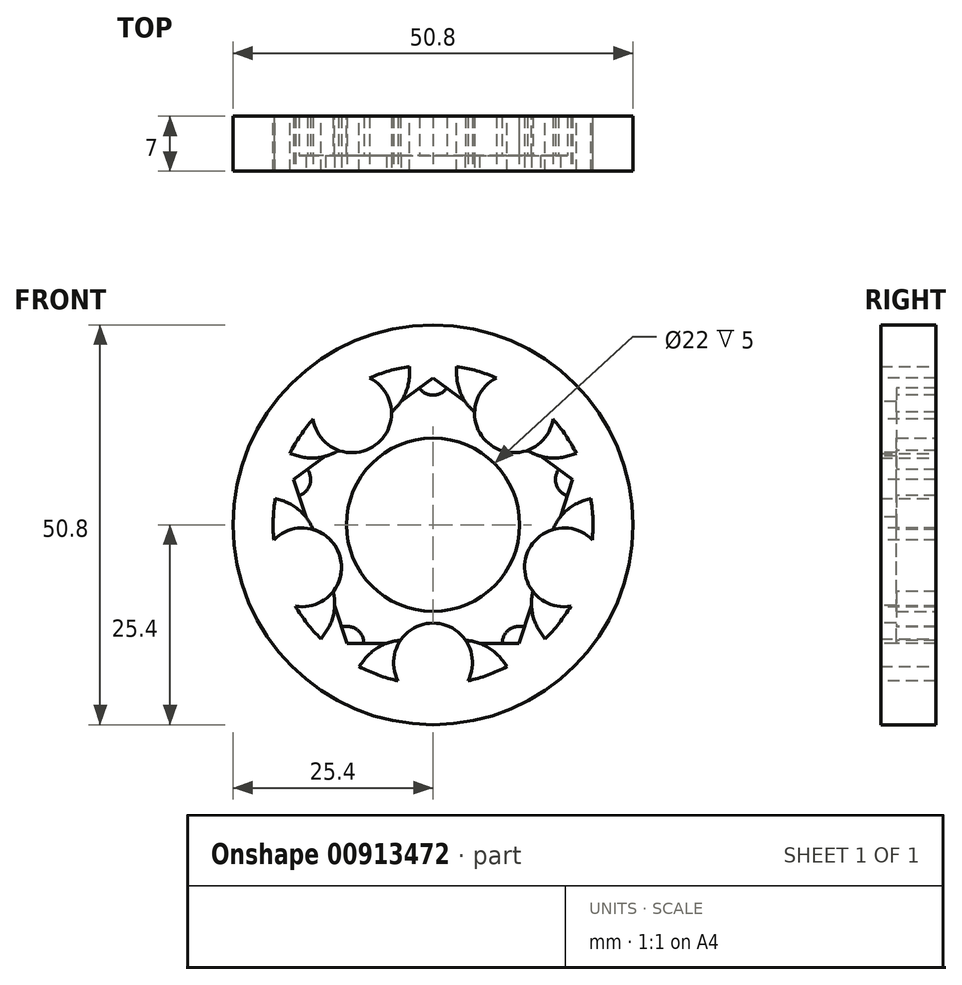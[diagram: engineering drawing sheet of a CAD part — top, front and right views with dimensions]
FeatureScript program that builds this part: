
annotation { "Feature Type Name" : "Feature", "Feature Type Description" : "" }
export const myFeature = defineFeature(function(context is Context, id is Id, definition is map)
    precondition{}
    {
        {
            var Q0;
            Q0=qCreatedBy(makeId("Front.planeOp"),FACE);
            var sketch = newSketch(context, id + "F0", { "sketchPlane" : qUnion([Q0])});
            skCircle(sketch, "E0", {"center": v(0, 0) * mm, "radius": 11 * mm});
            skCircle(sketch, "E1", {"center": v(0, 0) * mm, "radius": 25.4 * mm});
            skArc(sketch, "E2.0", {"start": v(-3, 20.1) * mm, "mid": v(-11.94, 16.44) * mm, "end": v(-18.19, 9.06) * mm});
            skArc(sketch, "E3.0", {"start": v(-6.57, 13.49) * mm, "mid": v(-8.82, 12.14) * mm, "end": v(-10.8, 10.41) * mm});
            skLineSegment(sketch, "E4.0", {"start": v(-3, 20.1) * mm, "end": v(-3, 19.2) * mm});
            skLineSegment(sketch, "E5.0", {"start": v(3, 20.1) * mm, "end": v(3, 19.2) * mm});
            skPoint(sketch, "E6.orphan", {"position": v(0, 22.5) * mm});
            skPoint(sketch, "E7.visualSharp", {"position": v(3, 14.7) * mm});
            skArc(sketch, "E7.filletArc", {"start": v(3, 19.2) * mm, "mid": v(3.97, 15.83) * mm, "end": v(6.57, 13.49) * mm});
            skPoint(sketch, "E8.visualSharp", {"position": v(-3, 14.7) * mm});
            skArc(sketch, "E8.filletArc", {"start": v(-6.57, 13.49) * mm, "mid": v(-3.97, 15.83) * mm, "end": v(-3, 19.2) * mm});
            skLineSegment(sketch, "E9.1.0", {"start": v(-18.19, 9.06) * mm, "end": v(-17.33, 8.78) * mm});
            skArc(sketch, "E9.1.1", {"start": v(-17.33, 8.78) * mm, "mid": v(-13.83, 8.66) * mm, "end": v(-10.8, 10.41) * mm});
            skLineSegment(sketch, "E9.1.2", {"start": v(-20.04, 3.36) * mm, "end": v(-19.18, 3.08) * mm});
            skArc(sketch, "E9.1.3", {"start": v(-14.86, -2.08) * mm, "mid": v(-16.28, 1.12) * mm, "end": v(-19.18, 3.08) * mm});
            skLineSegment(sketch, "E9.2.0", {"start": v(-14.24, -14.5) * mm, "end": v(-13.7, -13.76) * mm});
            skArc(sketch, "E9.2.1", {"start": v(-13.7, -13.76) * mm, "mid": v(-12.51, -10.47) * mm, "end": v(-13.24, -7.05) * mm});
            skLineSegment(sketch, "E9.2.2", {"start": v(-9.39, -18.02) * mm, "end": v(-8.85, -17.3) * mm});
            skArc(sketch, "E9.2.3", {"start": v(-2.61, -14.77) * mm, "mid": v(-6.1, -15.14) * mm, "end": v(-8.85, -17.3) * mm});
            skLineSegment(sketch, "E9.3.0", {"start": v(9.39, -18.02) * mm, "end": v(8.85, -17.3) * mm});
            skArc(sketch, "E9.3.1", {"start": v(8.85, -17.3) * mm, "mid": v(6.1, -15.14) * mm, "end": v(2.61, -14.77) * mm});
            skLineSegment(sketch, "E9.3.2", {"start": v(14.24, -14.5) * mm, "end": v(13.7, -13.76) * mm});
            skArc(sketch, "E9.3.3", {"start": v(13.24, -7.05) * mm, "mid": v(12.51, -10.47) * mm, "end": v(13.7, -13.76) * mm});
            skLineSegment(sketch, "E9.4.0", {"start": v(20.04, 3.36) * mm, "end": v(19.18, 3.08) * mm});
            skArc(sketch, "E9.4.1", {"start": v(19.18, 3.08) * mm, "mid": v(16.28, 1.12) * mm, "end": v(14.86, -2.08) * mm});
            skLineSegment(sketch, "E9.4.2", {"start": v(18.19, 9.06) * mm, "end": v(17.33, 8.78) * mm});
            skArc(sketch, "E9.4.3", {"start": v(10.8, 10.41) * mm, "mid": v(13.83, 8.66) * mm, "end": v(17.33, 8.78) * mm});
            skArc(sketch, "E10.trimOffspring", {"start": v(-14.86, -2.08) * mm, "mid": v(-14.27, -4.64) * mm, "end": v(-13.24, -7.05) * mm});
            skArc(sketch, "E11.trimOffspring", {"start": v(-2.61, -14.77) * mm, "mid": v(0, -15) * mm, "end": v(2.61, -14.77) * mm});
            skArc(sketch, "E12.trimOffspring", {"start": v(13.24, -7.05) * mm, "mid": v(14.27, -4.64) * mm, "end": v(14.86, -2.08) * mm});
            skArc(sketch, "E13.trimOffspring", {"start": v(18.19, 9.06) * mm, "mid": v(11.94, 16.44) * mm, "end": v(3, 20.1) * mm});
            skArc(sketch, "E14.trimOffspring", {"start": v(10.8, 10.41) * mm, "mid": v(8.82, 12.14) * mm, "end": v(6.57, 13.49) * mm});
            skArc(sketch, "E15.trimOffspring", {"start": v(14.24, -14.5) * mm, "mid": v(19.33, -6.28) * mm, "end": v(20.04, 3.36) * mm});
            skArc(sketch, "E16.trimOffspring", {"start": v(-9.39, -18.02) * mm, "mid": v(0, -20.32) * mm, "end": v(9.39, -18.02) * mm});
            skArc(sketch, "E17.trimOffspring", {"start": v(-20.04, 3.36) * mm, "mid": v(-19.33, -6.28) * mm, "end": v(-14.24, -14.5) * mm});
            skSolve(sketch);
        }
        {
            var Q0;
            Q0=makeQuery(id+"F0.imprint","IMPRINT",FACE,{"disambiguationData":[TD([[makeQuery(id+"F0.imprint","IMPRINT",EDGE,{"derivedFrom":sQuery(id+"F0.wireOp",EDGE,"E0")}),-1.0]])]});
            extrude(context, id + "F1", {"entities" : qUnion([Q0]), "endBound" : BoundingType.SYMMETRIC, "depth" : 7 * mm, "offsetDistance" : 25.4 * mm});
        }
        {
            var Q0;
            Q0=makeQuery(id+"F1.opExtrude","CAP_FACE",FACE,{"disambiguationData":[OSD([sQuery(id+"F0.wireOp",EDGE,"E0"),sQuery(id+"F0.wireOp",EDGE,"E1"),sQuery(id+"F0.wireOp",EDGE,"E2.0"),sQuery(id+"F0.wireOp",EDGE,"E3.0"),sQuery(id+"F0.wireOp",EDGE,"E4.0"),sQuery(id+"F0.wireOp",EDGE,"E5.0"),sQuery(id+"F0.wireOp",EDGE,"E7.filletArc"),sQuery(id+"F0.wireOp",EDGE,"E8.filletArc"),sQuery(id+"F0.wireOp",EDGE,"E9.1.0"),sQuery(id+"F0.wireOp",EDGE,"E9.1.1"),sQuery(id+"F0.wireOp",EDGE,"E9.1.2"),sQuery(id+"F0.wireOp",EDGE,"E9.1.3"),sQuery(id+"F0.wireOp",EDGE,"E9.2.0"),sQuery(id+"F0.wireOp",EDGE,"E9.2.1"),sQuery(id+"F0.wireOp",EDGE,"E9.2.2"),sQuery(id+"F0.wireOp",EDGE,"E9.2.3"),sQuery(id+"F0.wireOp",EDGE,"E9.3.0"),sQuery(id+"F0.wireOp",EDGE,"E9.3.1"),sQuery(id+"F0.wireOp",EDGE,"E9.3.2"),sQuery(id+"F0.wireOp",EDGE,"E9.3.3"),sQuery(id+"F0.wireOp",EDGE,"E9.4.0"),sQuery(id+"F0.wireOp",EDGE,"E9.4.1"),sQuery(id+"F0.wireOp",EDGE,"E9.4.2"),sQuery(id+"F0.wireOp",EDGE,"E9.4.3"),sQuery(id+"F0.wireOp",EDGE,"E10.trimOffspring"),sQuery(id+"F0.wireOp",EDGE,"E11.trimOffspring"),sQuery(id+"F0.wireOp",EDGE,"E12.trimOffspring"),sQuery(id+"F0.wireOp",EDGE,"E13.trimOffspring"),sQuery(id+"F0.wireOp",EDGE,"E14.trimOffspring"),sQuery(id+"F0.wireOp",EDGE,"E15.trimOffspring"),sQuery(id+"F0.wireOp",EDGE,"E16.trimOffspring"),sQuery(id+"F0.wireOp",EDGE,"E17.trimOffspring")])],"isStart":false});
            var sketch = newSketch(context, id + "F2", { "sketchPlane" : qUnion([Q0])});
            skCircle(sketch, "E18.cCircle", {"center": v(0, 0) * mm, "radius": 18.62 * mm, "construction": true});
            skLineSegment(sketch, "E18.0", {"start": v(10.95, -15.07) * mm, "end": v(-10.95, -15.07) * mm});
            skLineSegment(sketch, "E18.1", {"start": v(-10.95, -15.07) * mm, "end": v(-17.71, 5.75) * mm});
            skLineSegment(sketch, "E18.2", {"start": v(-17.71, 5.75) * mm, "end": v(0, 18.62) * mm});
            skLineSegment(sketch, "E18.3", {"start": v(0, 18.62) * mm, "end": v(17.71, 5.75) * mm});
            skLineSegment(sketch, "E18.4", {"start": v(17.71, 5.75) * mm, "end": v(10.95, -15.07) * mm});
            skSolve(sketch);
        }
        {
            var Q0;
            Q0=makeQuery(id+"F2.imprint","IMPRINT",FACE,{"disambiguationData":[TD([[makeQuery(id+"F2.imprint","IMPRINT",EDGE,{"derivedFrom":makeQuery(id+"F1.opExtrude","CAP_EDGE",EDGE,{"disambiguationData":[OSD([sQuery(id+"F0.wireOp",EDGE,"E0")])],"isStart":false})}),-1.0]])]});
            extrude(context, id + "F3", {"entities" : qUnion([Q0]), "operationType" : NewBodyOperationType.REMOVE, "oppositeDirection" : true, "depth" : 2 * mm, "offsetDistance" : 25.4 * mm});
        }
        {
            var Q0;
            Q0=makeQuery(id+"F3.boolean.opBoolean","COPY",FACE,{"derivedFrom":makeQuery(id+"F3.opExtrude","CAP_FACE",FACE,{"disambiguationData":[OSD([sQuery(id+"F0.wireOp",EDGE,"E0"),sQuery(id+"F0.wireOp",EDGE,"E3.0"),sQuery(id+"F0.wireOp",EDGE,"E7.filletArc"),sQuery(id+"F0.wireOp",EDGE,"E8.filletArc"),sQuery(id+"F0.wireOp",EDGE,"E9.1.1"),sQuery(id+"F0.wireOp",EDGE,"E9.1.3"),sQuery(id+"F0.wireOp",EDGE,"E9.2.1"),sQuery(id+"F0.wireOp",EDGE,"E9.2.3"),sQuery(id+"F0.wireOp",EDGE,"E9.3.1"),sQuery(id+"F0.wireOp",EDGE,"E9.3.3"),sQuery(id+"F0.wireOp",EDGE,"E9.4.1"),sQuery(id+"F0.wireOp",EDGE,"E9.4.3"),sQuery(id+"F0.wireOp",EDGE,"E10.trimOffspring"),sQuery(id+"F0.wireOp",EDGE,"E11.trimOffspring"),sQuery(id+"F0.wireOp",EDGE,"E12.trimOffspring"),sQuery(id+"F0.wireOp",EDGE,"E14.trimOffspring"),sQuery(id+"F2.wireOp",EDGE,"E18.0"),sQuery(id+"F2.wireOp",EDGE,"E18.1"),sQuery(id+"F2.wireOp",EDGE,"E18.2"),sQuery(id+"F2.wireOp",EDGE,"E18.3"),sQuery(id+"F2.wireOp",EDGE,"E18.4")])],"isStart":false})});
            var sketch = newSketch(context, id + "F4", { "sketchPlane" : qUnion([Q0])});
            skCircle(sketch, "E19", {"center": v(0, 18.62) * mm, "radius": 2.16 * mm});
            skCircle(sketch, "E20.1.0", {"center": v(-17.71, 5.75) * mm, "radius": 2.16 * mm});
            skCircle(sketch, "E20.2.0", {"center": v(-10.95, -15.07) * mm, "radius": 2.16 * mm});
            skCircle(sketch, "E20.3.0", {"center": v(10.95, -15.07) * mm, "radius": 2.16 * mm});
            skCircle(sketch, "E20.4.0", {"center": v(17.71, 5.75) * mm, "radius": 2.16 * mm});
            skPoint(sketch, "E20.center", {"position": v(0, 0) * mm});
            skSolve(sketch);
        }
        {
            var Q0;
            {var subQ0=sQuery(id+"F4.wireOp",EDGE,"E20.1.0");var subQ1=sQuery(id+"F2.wireOp",EDGE,"E18.2");var subQ2=sQuery(id+"F2.wireOp",EDGE,"E18.1");var subQ3=makeQuery(id+"F2.imprint","INTERSECT",VERTEX,{"derivedFrom":[subQ2,subQ1]});var subQ4=makeQuery(id+"F3.boolean.opBoolean","COPY",EDGE,{"derivedFrom":makeQuery(id+"F3.opExtrude","CAP_EDGE",EDGE,{"disambiguationData":[OSD([subQ2]),TDD([makeQuery(id+"F2.imprint","IMPRINT",EDGE,{"disambiguationData":[TD([[subQ3,1.0]])],"derivedFrom":subQ2})])],"isStart":false})});var subQ5=makeQuery(id+"F4.imprint","INTERSECT",VERTEX,{"derivedFrom":[subQ4,subQ0]});Q0=makeQuery(id+"F4.imprint","IMPRINT",FACE,{"disambiguationData":[TD([[makeQuery(id+"F4.imprint","IMPRINT",EDGE,{"disambiguationData":[TD([[subQ5,-1.0]])],"derivedFrom":subQ0}),1.0]])]});}
            var Q1;
            {var subQ0=sQuery(id+"F4.wireOp",EDGE,"E20.2.0");var subQ1=sQuery(id+"F2.wireOp",EDGE,"E18.1");var subQ2=sQuery(id+"F2.wireOp",EDGE,"E18.0");var subQ3=makeQuery(id+"F2.imprint","INTERSECT",VERTEX,{"derivedFrom":[subQ2,subQ1]});var subQ4=makeQuery(id+"F3.boolean.opBoolean","COPY",EDGE,{"derivedFrom":makeQuery(id+"F3.opExtrude","CAP_EDGE",EDGE,{"disambiguationData":[OSD([subQ2]),TDD([makeQuery(id+"F2.imprint","IMPRINT",EDGE,{"disambiguationData":[TD([[subQ3,1.0]])],"derivedFrom":subQ2})])],"isStart":false})});var subQ5=makeQuery(id+"F4.imprint","INTERSECT",VERTEX,{"derivedFrom":[subQ4,subQ0]});Q1=makeQuery(id+"F4.imprint","IMPRINT",FACE,{"disambiguationData":[TD([[makeQuery(id+"F4.imprint","IMPRINT",EDGE,{"disambiguationData":[TD([[subQ5,-1.0]])],"derivedFrom":subQ0}),1.0]])]});}
            var Q2;
            {var subQ0=sQuery(id+"F4.wireOp",EDGE,"E20.3.0");var subQ1=sQuery(id+"F2.wireOp",EDGE,"E18.4");var subQ2=sQuery(id+"F2.wireOp",EDGE,"E18.0");var subQ3=makeQuery(id+"F2.imprint","INTERSECT",VERTEX,{"derivedFrom":[subQ2,subQ1]});var subQ4=makeQuery(id+"F3.boolean.opBoolean","COPY",EDGE,{"derivedFrom":makeQuery(id+"F3.opExtrude","CAP_EDGE",EDGE,{"disambiguationData":[OSD([subQ2]),TDD([makeQuery(id+"F2.imprint","IMPRINT",EDGE,{"disambiguationData":[TD([[subQ3,-1.0]])],"derivedFrom":subQ2})])],"isStart":false})});var subQ5=makeQuery(id+"F4.imprint","INTERSECT",VERTEX,{"derivedFrom":[subQ4,subQ0]});Q2=makeQuery(id+"F4.imprint","IMPRINT",FACE,{"disambiguationData":[TD([[makeQuery(id+"F4.imprint","IMPRINT",EDGE,{"disambiguationData":[TD([[subQ5,1.0]])],"derivedFrom":subQ0}),1.0]])]});}
            var Q3;
            {var subQ0=sQuery(id+"F4.wireOp",EDGE,"E20.4.0");var subQ1=sQuery(id+"F2.wireOp",EDGE,"E18.4");var subQ2=sQuery(id+"F2.wireOp",EDGE,"E18.3");var subQ3=makeQuery(id+"F2.imprint","INTERSECT",VERTEX,{"derivedFrom":[subQ2,subQ1]});var subQ4=makeQuery(id+"F3.boolean.opBoolean","COPY",EDGE,{"derivedFrom":makeQuery(id+"F3.opExtrude","CAP_EDGE",EDGE,{"disambiguationData":[OSD([subQ2]),TDD([makeQuery(id+"F2.imprint","IMPRINT",EDGE,{"disambiguationData":[TD([[subQ3,1.0]])],"derivedFrom":subQ2})])],"isStart":false})});var subQ5=makeQuery(id+"F4.imprint","INTERSECT",VERTEX,{"derivedFrom":[subQ4,subQ0]});Q3=makeQuery(id+"F4.imprint","IMPRINT",FACE,{"disambiguationData":[TD([[makeQuery(id+"F4.imprint","IMPRINT",EDGE,{"disambiguationData":[TD([[subQ5,-1.0]])],"derivedFrom":subQ0}),1.0]])]});}
            var Q4;
            {var subQ0=sQuery(id+"F4.wireOp",EDGE,"E19");var subQ1=sQuery(id+"F2.wireOp",EDGE,"E18.3");var subQ2=sQuery(id+"F2.wireOp",EDGE,"E18.2");var subQ3=makeQuery(id+"F2.imprint","INTERSECT",VERTEX,{"derivedFrom":[subQ2,subQ1]});var subQ4=makeQuery(id+"F3.boolean.opBoolean","COPY",EDGE,{"derivedFrom":makeQuery(id+"F3.opExtrude","CAP_EDGE",EDGE,{"disambiguationData":[OSD([subQ2]),TDD([makeQuery(id+"F2.imprint","IMPRINT",EDGE,{"disambiguationData":[TD([[subQ3,1.0]])],"derivedFrom":subQ2})])],"isStart":false})});var subQ5=makeQuery(id+"F4.imprint","INTERSECT",VERTEX,{"derivedFrom":[subQ4,subQ0]});Q4=makeQuery(id+"F4.imprint","IMPRINT",FACE,{"disambiguationData":[TD([[makeQuery(id+"F4.imprint","IMPRINT",EDGE,{"disambiguationData":[TD([[subQ5,-1.0]])],"derivedFrom":subQ0}),1.0]])]});}
            extrude(context, id + "F5", {"entities" : qUnion([Q0, Q1, Q2, Q3, Q4]), "operationType" : NewBodyOperationType.REMOVE, "oppositeDirection" : true, "depth" : 25.4 * mm, "offsetDistance" : 25.4 * mm});
        }
        {
            var Q0;
            Q0=makeQuery(id+"F1.opExtrude","CAP_FACE",FACE,{"disambiguationData":[OSD([sQuery(id+"F0.wireOp",EDGE,"E0"),sQuery(id+"F0.wireOp",EDGE,"E1"),sQuery(id+"F0.wireOp",EDGE,"E2.0"),sQuery(id+"F0.wireOp",EDGE,"E3.0"),sQuery(id+"F0.wireOp",EDGE,"E4.0"),sQuery(id+"F0.wireOp",EDGE,"E5.0"),sQuery(id+"F0.wireOp",EDGE,"E7.filletArc"),sQuery(id+"F0.wireOp",EDGE,"E8.filletArc"),sQuery(id+"F0.wireOp",EDGE,"E9.1.0"),sQuery(id+"F0.wireOp",EDGE,"E9.1.1"),sQuery(id+"F0.wireOp",EDGE,"E9.1.2"),sQuery(id+"F0.wireOp",EDGE,"E9.1.3"),sQuery(id+"F0.wireOp",EDGE,"E9.2.0"),sQuery(id+"F0.wireOp",EDGE,"E9.2.1"),sQuery(id+"F0.wireOp",EDGE,"E9.2.2"),sQuery(id+"F0.wireOp",EDGE,"E9.2.3"),sQuery(id+"F0.wireOp",EDGE,"E9.3.0"),sQuery(id+"F0.wireOp",EDGE,"E9.3.1"),sQuery(id+"F0.wireOp",EDGE,"E9.3.2"),sQuery(id+"F0.wireOp",EDGE,"E9.3.3"),sQuery(id+"F0.wireOp",EDGE,"E9.4.0"),sQuery(id+"F0.wireOp",EDGE,"E9.4.1"),sQuery(id+"F0.wireOp",EDGE,"E9.4.2"),sQuery(id+"F0.wireOp",EDGE,"E9.4.3"),sQuery(id+"F0.wireOp",EDGE,"E10.trimOffspring"),sQuery(id+"F0.wireOp",EDGE,"E11.trimOffspring"),sQuery(id+"F0.wireOp",EDGE,"E12.trimOffspring"),sQuery(id+"F0.wireOp",EDGE,"E13.trimOffspring"),sQuery(id+"F0.wireOp",EDGE,"E14.trimOffspring"),sQuery(id+"F0.wireOp",EDGE,"E15.trimOffspring"),sQuery(id+"F0.wireOp",EDGE,"E16.trimOffspring"),sQuery(id+"F0.wireOp",EDGE,"E17.trimOffspring")])],"isStart":false});
            var sketch = newSketch(context, id + "F6", { "sketchPlane" : qUnion([Q0])});
            skCircle(sketch, "E21", {"center": v(-10.28, 14.16) * mm, "radius": 5 * mm});
            skPoint(sketch, "E22.end.orphan", {"position": v(-11.94, 16.44) * mm});
            skCircle(sketch, "E23.1.0", {"center": v(-16.64, -5.4) * mm, "radius": 5 * mm});
            skCircle(sketch, "E23.2.0", {"center": v(0, -17.5) * mm, "radius": 5 * mm});
            skCircle(sketch, "E23.3.0", {"center": v(16.64, -5.4) * mm, "radius": 5 * mm});
            skCircle(sketch, "E23.4.0", {"center": v(10.28, 14.16) * mm, "radius": 5 * mm});
            skPoint(sketch, "E23.center", {"position": v(0, 0) * mm});
            skSolve(sketch);
        }
        {
            var Q0;
            Q0 = qSketchRegion(id + "F6", true);
            extrude(context, id + "F7", {"entities" : qUnion([Q0]), "operationType" : NewBodyOperationType.ADD, "oppositeDirection" : true, "depth" : 7 * mm, "offsetDistance" : 25.4 * mm});
        }
    });
